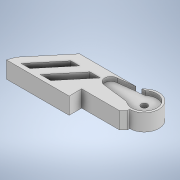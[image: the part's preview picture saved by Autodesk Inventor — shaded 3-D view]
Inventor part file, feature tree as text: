
AUTODESK INVENTOR PART (.ipt)
format: ipt  version: 2021 (Build 250183000, 183)  size: 186,880 bytes
history: native  units: mm
features: extrude x5, sketch x5, other x1, chamfer x1
ambient origin geometry x8: Origin, YZ Plane, XZ Plane, XY Plane, X Axis, Y Axis, Z Axis, Center Point
bodies: Body1 (feature_tree)
feature tree (12):
  other  "Sólido1"
  extrude  "Extrusión1"  Depth=6.0mm
  extrude  "Extrusión6"  Depth=5.0mm
  extrude  "Extrusión7"  Depth=5.0mm
  chamfer  "Chaflán1"  Distance=5.0mm
  extrude  "Extrusión9"  Depth=5.0mm
  extrude  "Extrusión10"  Depth=5.0mm
  sketch  "Boceto1"  dims[d8=6.0mm d9=0.5mm]
  sketch  "Boceto6"  dims[d10=8.0mm d11=0.0mm d28=5.0mm]
  sketch  "Boceto7"  dims[d29=5.0mm d30=5.0mm]
  sketch  "Boceto9"  dims[d31=5.0mm]
  sketch  "Boceto10"  dims[d32=5.0mm d33=5.0mm d34=5.0mm d35=5.0mm d36=5.0mm d37=10.0mm d38=0.0mm d39=10.0mm d40=0.0mm d44=2.0mm d45=2.0mm d46=45.0deg d47=6.0mm d48=4.0mm d49=0.0mm d50=12.0mm d51=19.0mm d52=4.5mm d53=9.0mm d54=3.0mm d55=2.0mm d56=0.0mm d25=0.5mm d26=0.872665mm d27=0.5mm]
